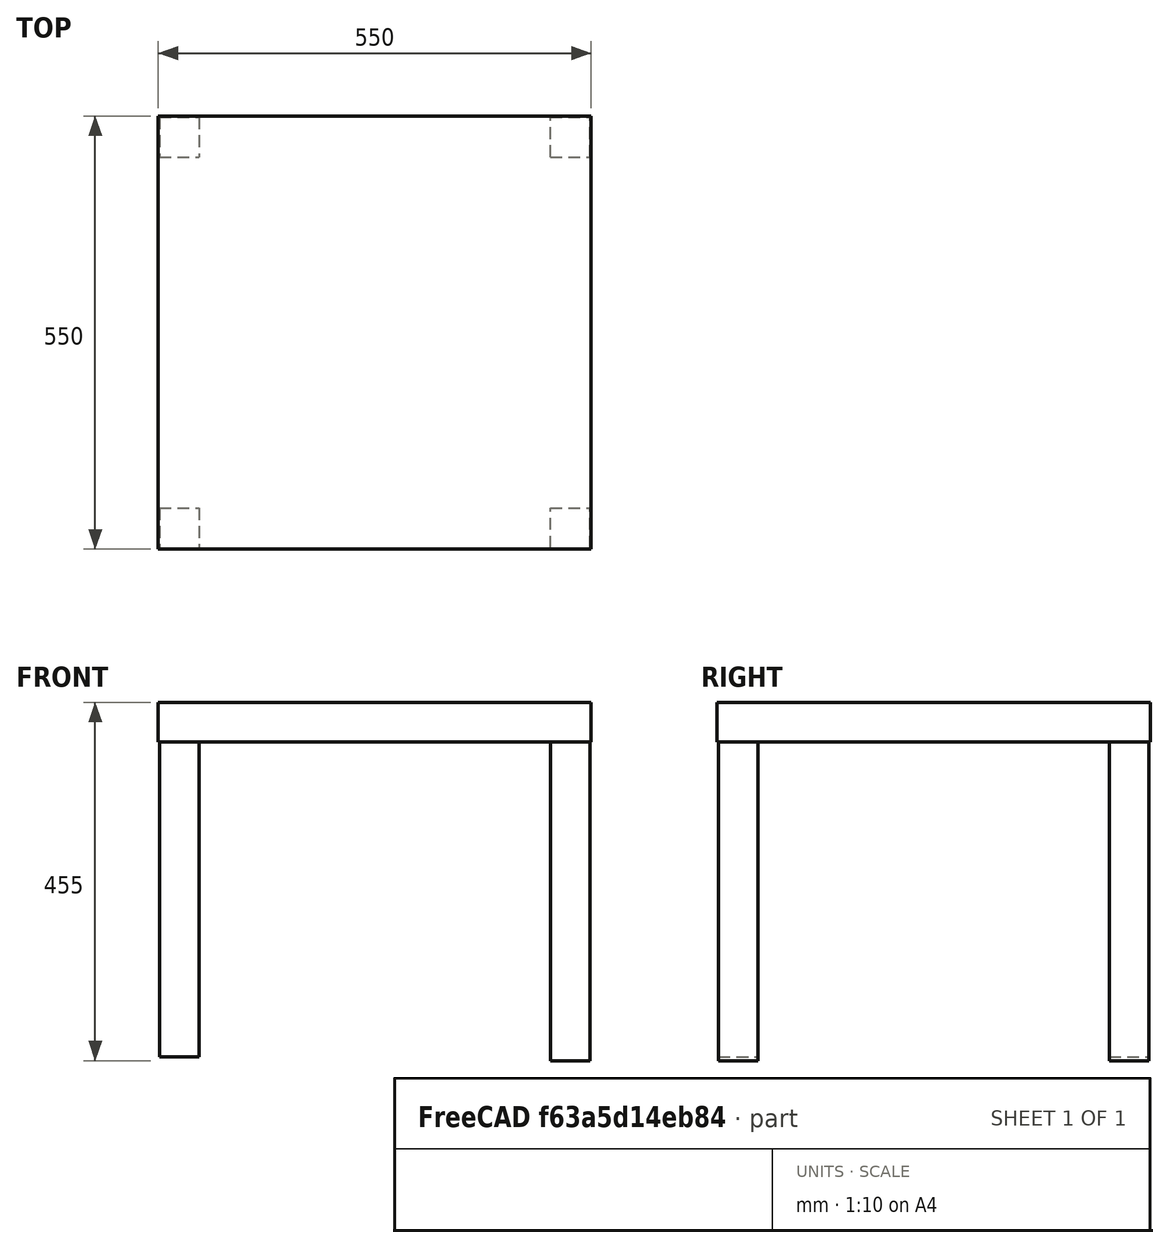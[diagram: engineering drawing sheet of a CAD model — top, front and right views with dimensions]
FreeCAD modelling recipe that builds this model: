
FCSTD DOCUMENT  (FreeCAD 0.16R6706 (Git))
Label: IKEA_Lack_550_550_450
License: All rights reserved
LicenseURL: http://en.wikipedia.org/wiki/All_rights_reserved
objects: Part::Box×5, Part::MultiFuse×1
note: 6 computed .brp shape members not serialized (recipe doc carries the construction recipe); baked Part::Feature solids carry a one-line shape summary decoded from their .brp

FEATURE [Part::Box] Box
  Height = 50
  Length = 550
  Placement = pos=(0,0,400) rot=(0,0,1;0rad)
  Width = 550
FEATURE [Part::Box] Box001
  Height = 405
  Length = 50.5
  Placement = pos=(1.5,1.5,0) rot=(0,0,1;0rad)
  Width = 50.5
FEATURE [Part::Box] Box002
  Height = 405
  Length = 50.5
  Placement = pos=(1.5,498,0) rot=(0,0,1;0rad)
  Width = 50.5
FEATURE [Part::Box] Box003
  Height = 405
  Length = 50.5
  Placement = pos=(498,1.5,-5) rot=(0,0,1;0rad)
  Width = 50.5
FEATURE [Part::Box] Box004
  Height = 405
  Length = 50.5
  Placement = pos=(498,498,-5) rot=(0,0,1;0rad)
  Width = 50.5
FEATURE [Part::MultiFuse] Fusion  label="IKEA_Lack_550_550_450"
  Shapes = -> [Box001,Box002,Box003,Box004,Box]
